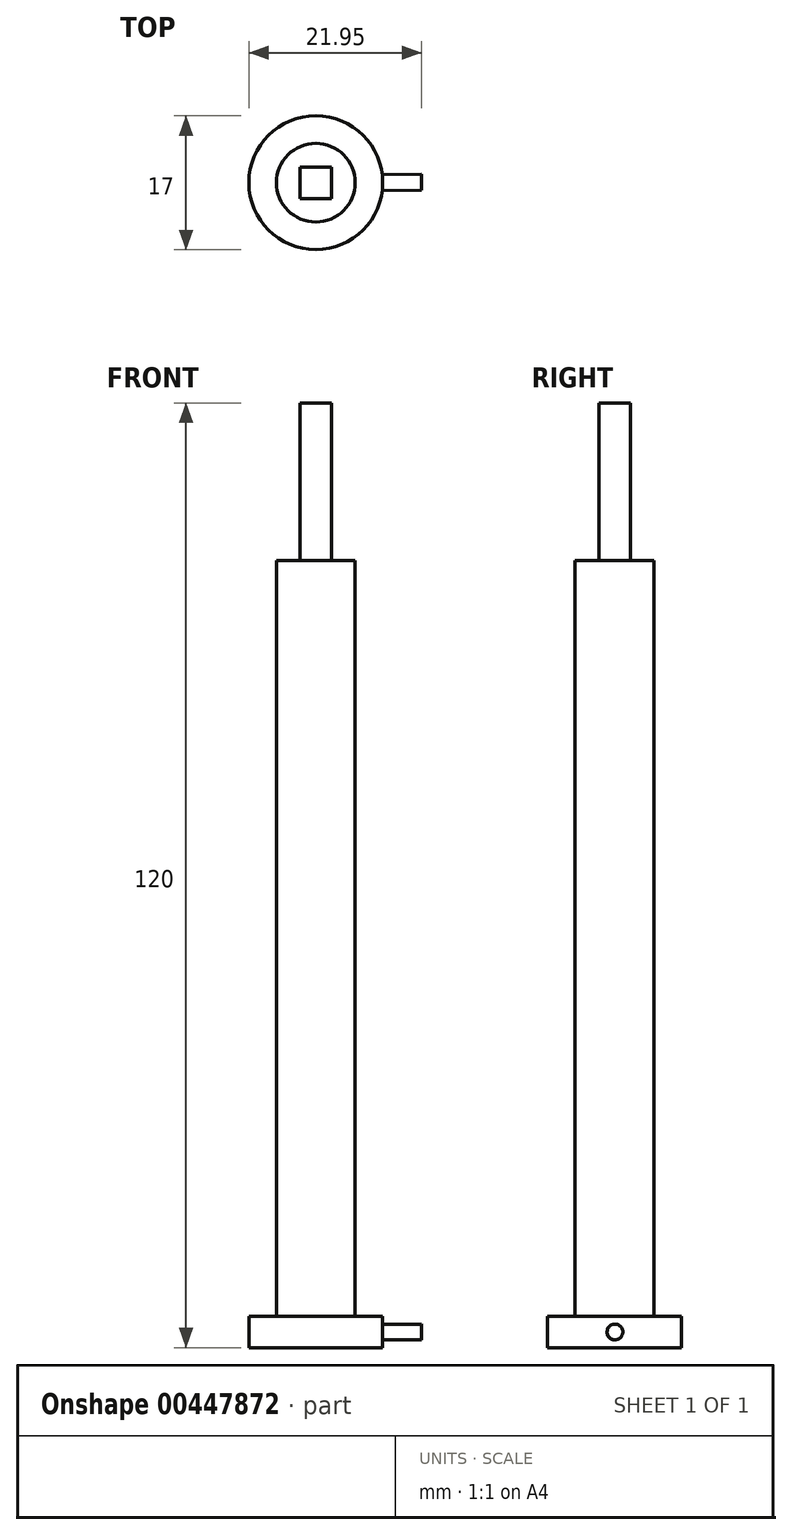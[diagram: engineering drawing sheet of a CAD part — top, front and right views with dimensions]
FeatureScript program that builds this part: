
annotation { "Feature Type Name" : "Feature", "Feature Type Description" : "" }
export const myFeature = defineFeature(function(context is Context, id is Id, definition is map)
    precondition{}
    {
        {
            var Q0;
            Q0=qCreatedBy(makeId("Top.planeOp"),FACE);
            var sketch = newSketch(context, id + "F0", { "sketchPlane" : qUnion([Q0])});
            skCircle(sketch, "E0", {"center": v(0, 0) * mm, "radius": 8.5 * mm});
            skSolve(sketch);
        }
        {
            var Q0;
            Q0=qSketchRegion(id+"F0",true);
            extrude(context, id + "F1", {"entities" : qUnion([Q0]), "depth" : 4 * mm});
        }
        {
            var Q0;
            Q0=qCreatedBy(makeId("Top.planeOp"),FACE);
            var sketch = newSketch(context, id + "F2", { "sketchPlane" : qUnion([Q0])});
            skCircle(sketch, "E1", {"center": v(0, 0) * mm, "radius": 5 * mm});
            skSolve(sketch);
        }
        {
            var Q0;
            Q0=qSketchRegion(id+"F2",true);
            extrude(context, id + "F3", {"entities" : qUnion([Q0]), "operationType" : NewBodyOperationType.ADD, "depth" : 100 * mm});
        }
        {
            var Q0;
            Q0=makeQuery(id+"F3.opExtrude","CAP_FACE",FACE,{"disambiguationData":[OSD([sQuery(id+"F2.wireOp",EDGE,"E1")])],"isStart":false});
            var sketch = newSketch(context, id + "F4", { "sketchPlane" : qUnion([Q0])});
            skLineSegment(sketch, "E2.bottom", {"start": v(-2, 2) * mm, "end": v(2, 2) * mm});
            skLineSegment(sketch, "E2.top", {"start": v(-2, -2) * mm, "end": v(2, -2) * mm});
            skLineSegment(sketch, "E2.left", {"start": v(-2, 2) * mm, "end": v(-2, -2) * mm});
            skLineSegment(sketch, "E2.right", {"start": v(2, 2) * mm, "end": v(2, -2) * mm});
            skSolve(sketch);
        }
        {
            var Q0;
            Q0=makeQuery(id+"F4.imprint","IMPRINT",FACE,{"disambiguationData":[TD([[makeQuery(id+"F4.imprint","IMPRINT",EDGE,{"derivedFrom":sQuery(id+"F4.wireOp",EDGE,"E2.bottom")}),-1.0]])]});
            extrude(context, id + "F5", {"entities" : qUnion([Q0]), "operationType" : NewBodyOperationType.ADD, "depth" : 20 * mm});
        }
        {
            var Q0;
            Q0=qCreatedBy(makeId("Top.planeOp"),FACE);
            var sketch = newSketch(context, id + "F6", { "sketchPlane" : qUnion([Q0])});
            skLineSegment(sketch, "E3.right", {"start": v(8.45, -0.9) * mm, "end": v(8.43, 1.1) * mm});
            skSolve(sketch);
        }
        {
            var Q0;
            Q0=sQuery(id+"F6.wireOp",EDGE,"E3.right");
            cPlane(context, id + "F7", {"entities" : qUnion([Q0]), "cplaneType" : CPlaneType.LINE_ANGLE, "offset" : 25 * mm, "angle" : 90 * degree, "width" : 150 * mm, "height" : 150 * mm});
        }
        {
            var Q0;
            Q0=qCreatedBy(id+"F7.planeOp",FACE);
            var sketch = newSketch(context, id + "F8", { "sketchPlane" : qUnion([Q0])});
            skCircle(sketch, "E4", {"center": v(-0.1, 2) * mm, "radius": 1 * mm});
            skSolve(sketch);
        }
        {
            var Q0;
            Q0=makeQuery(id+"F8.imprint","IMPRINT",FACE,{"disambiguationData":[TD([[makeQuery(id+"F8.imprint","IMPRINT",EDGE,{"derivedFrom":sQuery(id+"F8.wireOp",EDGE,"E4")}),1.0]])]});
            extrude(context, id + "F9", {"entities" : qUnion([Q0]), "operationType" : NewBodyOperationType.ADD, "depth" : 5 * mm});
        }
    });
